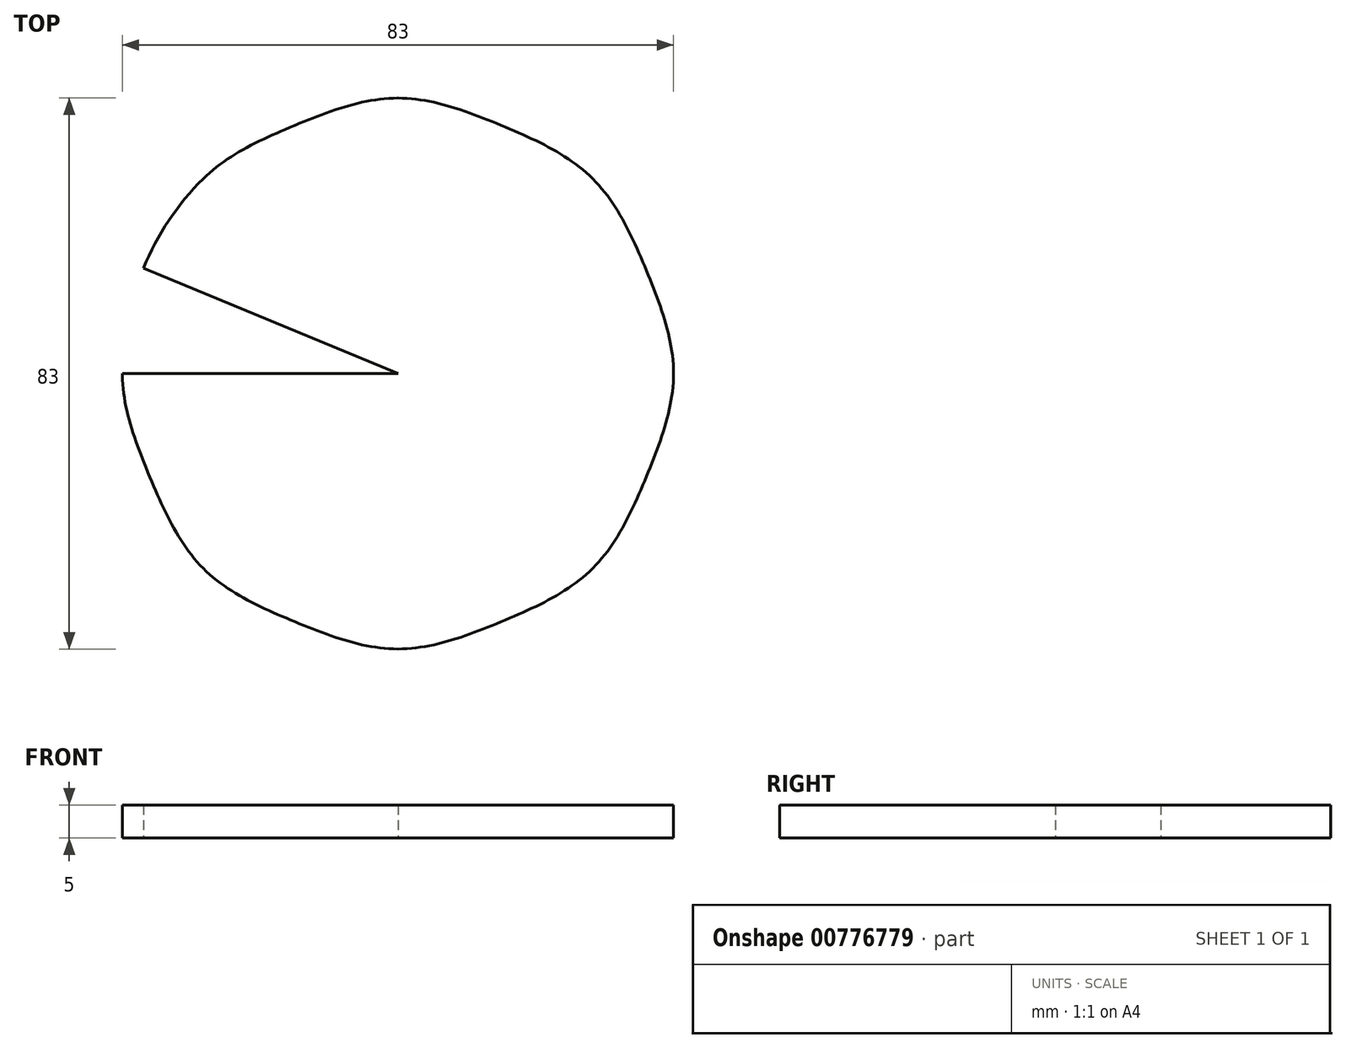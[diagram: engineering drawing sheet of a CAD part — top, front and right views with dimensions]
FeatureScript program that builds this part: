
annotation { "Feature Type Name" : "Feature", "Feature Type Description" : "" }
export const myFeature = defineFeature(function(context is Context, id is Id, definition is map)
    precondition{}
    {
        {
            var Q0;
            Q0=qCreatedBy(makeId("Top.planeOp"),FACE);
            var sketch = newSketch(context, id + "F0", { "sketchPlane" : qUnion([Q0])});
            skCircle(sketch, "E0", {"center": v(0, 0) * mm, "radius": 41.5 * mm});
            skCircle(sketch, "E1", {"center": v(0, 0) * mm, "radius": 40.5 * mm});
            skLineSegment(sketch, "E2", {"start": v(0, 0) * mm, "end": v(0, 41.5) * mm});
            skLineSegment(sketch, "E3.1.0", {"start": v(0, 0) * mm, "end": v(-15.88, 38.34) * mm});
            skLineSegment(sketch, "E3.2.0", {"start": v(0, 0) * mm, "end": v(-29.34, 29.34) * mm});
            skLineSegment(sketch, "E3.3.0", {"start": v(0, 0) * mm, "end": v(-38.34, 15.88) * mm});
            skLineSegment(sketch, "E3.4.0", {"start": v(0, 0) * mm, "end": v(-41.5, 0) * mm});
            skLineSegment(sketch, "E3.5.0", {"start": v(0, 0) * mm, "end": v(-38.34, -15.88) * mm});
            skLineSegment(sketch, "E3.6.0", {"start": v(0, 0) * mm, "end": v(-29.34, -29.34) * mm});
            skLineSegment(sketch, "E3.7.0", {"start": v(0, 0) * mm, "end": v(-15.88, -38.34) * mm});
            skLineSegment(sketch, "E3.8.0", {"start": v(0, 0) * mm, "end": v(0, -41.5) * mm});
            skLineSegment(sketch, "E3.9.0", {"start": v(0, 0) * mm, "end": v(15.88, -38.34) * mm});
            skLineSegment(sketch, "E3.10.0", {"start": v(0, 0) * mm, "end": v(29.34, -29.34) * mm});
            skLineSegment(sketch, "E3.11.0", {"start": v(0, 0) * mm, "end": v(38.34, -15.88) * mm});
            skLineSegment(sketch, "E3.12.0", {"start": v(0, 0) * mm, "end": v(41.5, 0) * mm});
            skLineSegment(sketch, "E3.13.0", {"start": v(0, 0) * mm, "end": v(38.34, 15.88) * mm});
            skLineSegment(sketch, "E3.14.0", {"start": v(0, 0) * mm, "end": v(29.34, 29.34) * mm});
            skLineSegment(sketch, "E3.15.0", {"start": v(0, 0) * mm, "end": v(15.88, 38.34) * mm});
            skFitSpline(sketch, "E4", {"points": [v(0, 41.5) * mm, v(15.5, 37.42) * mm, v(29.34, 29.34) * mm, v(37.42, 15.5) * mm, v(41.5, 0) * mm, v(37.42, -15.5) * mm, v(29.34, -29.34) * mm, v(15.5, -37.42) * mm, v(0, -41.5) * mm, v(-15.5, -37.42) * mm, v(-29.34, -29.34) * mm, v(-37.42, -15.5) * mm, v(-41.5, 0) * mm, v(-37.26, 15.88) * mm, v(-29.34, 29.34) * mm, v(-15.5, 37.42) * mm, v(0, 41.5) * mm]});
            skSolve(sketch);
        }
        {
            var Q0;
            {var subQ0=sQuery(id+"F0.wireOp",EDGE,"E4");var subQ1=sQuery(id+"F0.wireOp",EDGE,"E1");var subQ2=makeQuery(id+"F0.imprint","INTERSECT",VERTEX,{"disambiguationData":[OD(2.0)],"derivedFrom":[subQ1,subQ0]});Q0=makeQuery(id+"F0.imprint","IMPRINT",FACE,{"disambiguationData":[TD([[makeQuery(id+"F0.imprint","IMPRINT",EDGE,{"disambiguationData":[TD([[subQ2,-1.0]])],"derivedFrom":subQ1}),1.0]])]});}
            var Q1;
            {var subQ0=sQuery(id+"F0.wireOp",EDGE,"E3.2.0");var subQ1=sQuery(id+"F0.wireOp",EDGE,"E1");var subQ2=makeQuery(id+"F0.imprint","INTERSECT",VERTEX,{"derivedFrom":[subQ1,subQ0]});Q1=makeQuery(id+"F0.imprint","IMPRINT",FACE,{"disambiguationData":[TD([[makeQuery(id+"F0.imprint","IMPRINT",EDGE,{"disambiguationData":[TD([[subQ2,-1.0]])],"derivedFrom":subQ1}),1.0]])]});}
            var Q2;
            {var subQ0=sQuery(id+"F0.wireOp",EDGE,"E2");var subQ1=sQuery(id+"F0.wireOp",EDGE,"E1");var subQ2=makeQuery(id+"F0.imprint","INTERSECT",VERTEX,{"derivedFrom":[subQ1,subQ0]});Q2=makeQuery(id+"F0.imprint","IMPRINT",FACE,{"disambiguationData":[TD([[makeQuery(id+"F0.imprint","IMPRINT",EDGE,{"disambiguationData":[TD([[subQ2,-1.0]])],"derivedFrom":subQ1}),1.0]])]});}
            var Q3;
            {var subQ0=sQuery(id+"F0.wireOp",EDGE,"E4");var subQ1=sQuery(id+"F0.wireOp",EDGE,"E1");var subQ2=makeQuery(id+"F0.imprint","INTERSECT",VERTEX,{"disambiguationData":[OD(1.0)],"derivedFrom":[subQ1,subQ0]});Q3=makeQuery(id+"F0.imprint","IMPRINT",FACE,{"disambiguationData":[TD([[makeQuery(id+"F0.imprint","IMPRINT",EDGE,{"disambiguationData":[TD([[subQ2,-1.0]])],"derivedFrom":subQ1}),1.0]])]});}
            var Q4;
            {var subQ0=sQuery(id+"F0.wireOp",EDGE,"E4");var subQ1=sQuery(id+"F0.wireOp",EDGE,"E1");var subQ2=makeQuery(id+"F0.imprint","INTERSECT",VERTEX,{"disambiguationData":[OD(0.0)],"derivedFrom":[subQ1,subQ0]});Q4=makeQuery(id+"F0.imprint","IMPRINT",FACE,{"disambiguationData":[TD([[makeQuery(id+"F0.imprint","IMPRINT",EDGE,{"disambiguationData":[TD([[subQ2,-1.0]])],"derivedFrom":subQ1}),1.0]])]});}
            var Q5;
            {var subQ0=sQuery(id+"F0.wireOp",EDGE,"E3.12.0");var subQ1=sQuery(id+"F0.wireOp",EDGE,"E1");var subQ2=makeQuery(id+"F0.imprint","INTERSECT",VERTEX,{"derivedFrom":[subQ1,subQ0]});Q5=makeQuery(id+"F0.imprint","IMPRINT",FACE,{"disambiguationData":[TD([[makeQuery(id+"F0.imprint","IMPRINT",EDGE,{"disambiguationData":[TD([[subQ2,-1.0]])],"derivedFrom":subQ1}),1.0]])]});}
            var Q6;
            {var subQ0=sQuery(id+"F0.wireOp",EDGE,"E3.12.0");var subQ1=sQuery(id+"F0.wireOp",EDGE,"E1");var subQ2=makeQuery(id+"F0.imprint","INTERSECT",VERTEX,{"derivedFrom":[subQ1,subQ0]});Q6=makeQuery(id+"F0.imprint","IMPRINT",FACE,{"disambiguationData":[TD([[makeQuery(id+"F0.imprint","IMPRINT",EDGE,{"disambiguationData":[TD([[subQ2,1.0]])],"derivedFrom":subQ1}),1.0]])]});}
            var Q7;
            {var subQ0=sQuery(id+"F0.wireOp",EDGE,"E3.10.0");var subQ1=sQuery(id+"F0.wireOp",EDGE,"E1");var subQ2=makeQuery(id+"F0.imprint","INTERSECT",VERTEX,{"derivedFrom":[subQ1,subQ0]});Q7=makeQuery(id+"F0.imprint","IMPRINT",FACE,{"disambiguationData":[TD([[makeQuery(id+"F0.imprint","IMPRINT",EDGE,{"disambiguationData":[TD([[subQ2,-1.0]])],"derivedFrom":subQ1}),1.0]])]});}
            var Q8;
            {var subQ0=sQuery(id+"F0.wireOp",EDGE,"E4");var subQ1=sQuery(id+"F0.wireOp",EDGE,"E1");var subQ2=makeQuery(id+"F0.imprint","INTERSECT",VERTEX,{"disambiguationData":[OD(5.0)],"derivedFrom":[subQ1,subQ0]});Q8=makeQuery(id+"F0.imprint","IMPRINT",FACE,{"disambiguationData":[TD([[makeQuery(id+"F0.imprint","IMPRINT",EDGE,{"disambiguationData":[TD([[subQ2,-1.0]])],"derivedFrom":subQ1}),1.0]])]});}
            var Q9;
            {var subQ0=sQuery(id+"F0.wireOp",EDGE,"E3.8.0");var subQ1=sQuery(id+"F0.wireOp",EDGE,"E1");var subQ2=makeQuery(id+"F0.imprint","INTERSECT",VERTEX,{"derivedFrom":[subQ1,subQ0]});Q9=makeQuery(id+"F0.imprint","IMPRINT",FACE,{"disambiguationData":[TD([[makeQuery(id+"F0.imprint","IMPRINT",EDGE,{"disambiguationData":[TD([[subQ2,-1.0]])],"derivedFrom":subQ1}),1.0]])]});}
            var Q10;
            {var subQ0=sQuery(id+"F0.wireOp",EDGE,"E4");var subQ1=sQuery(id+"F0.wireOp",EDGE,"E1");var subQ2=makeQuery(id+"F0.imprint","INTERSECT",VERTEX,{"disambiguationData":[OD(3.0)],"derivedFrom":[subQ1,subQ0]});Q10=makeQuery(id+"F0.imprint","IMPRINT",FACE,{"disambiguationData":[TD([[makeQuery(id+"F0.imprint","IMPRINT",EDGE,{"disambiguationData":[TD([[subQ2,-1.0]])],"derivedFrom":subQ1}),1.0]])]});}
            var Q11;
            {var subQ0=sQuery(id+"F0.wireOp",EDGE,"E3.4.0");var subQ1=sQuery(id+"F0.wireOp",EDGE,"E1");var subQ2=makeQuery(id+"F0.imprint","INTERSECT",VERTEX,{"derivedFrom":[subQ1,subQ0]});Q11=makeQuery(id+"F0.imprint","IMPRINT",FACE,{"disambiguationData":[TD([[makeQuery(id+"F0.imprint","IMPRINT",EDGE,{"disambiguationData":[TD([[subQ2,-1.0]])],"derivedFrom":subQ1}),1.0]])]});}
            var Q12;
            {var subQ0=sQuery(id+"F0.wireOp",EDGE,"E4");var subQ1=sQuery(id+"F0.wireOp",EDGE,"E1");var subQ2=makeQuery(id+"F0.imprint","INTERSECT",VERTEX,{"disambiguationData":[OD(7.0)],"derivedFrom":[subQ1,subQ0]});Q12=makeQuery(id+"F0.imprint","IMPRINT",FACE,{"disambiguationData":[TD([[makeQuery(id+"F0.imprint","IMPRINT",EDGE,{"disambiguationData":[TD([[subQ2,-1.0]])],"derivedFrom":subQ1}),1.0]])]});}
            var Q13;
            {var subQ0=sQuery(id+"F0.wireOp",EDGE,"E4");var subQ1=sQuery(id+"F0.wireOp",EDGE,"E1");var subQ2=makeQuery(id+"F0.imprint","INTERSECT",VERTEX,{"disambiguationData":[OD(4.0)],"derivedFrom":[subQ1,subQ0]});Q13=makeQuery(id+"F0.imprint","IMPRINT",FACE,{"disambiguationData":[TD([[makeQuery(id+"F0.imprint","IMPRINT",EDGE,{"disambiguationData":[TD([[subQ2,-1.0]])],"derivedFrom":subQ1}),1.0]])]});}
            var Q14;
            {var subQ0=sQuery(id+"F0.wireOp",EDGE,"E3.6.0");var subQ1=sQuery(id+"F0.wireOp",EDGE,"E1");var subQ2=makeQuery(id+"F0.imprint","INTERSECT",VERTEX,{"derivedFrom":[subQ1,subQ0]});Q14=makeQuery(id+"F0.imprint","IMPRINT",FACE,{"disambiguationData":[TD([[makeQuery(id+"F0.imprint","IMPRINT",EDGE,{"disambiguationData":[TD([[subQ2,-1.0]])],"derivedFrom":subQ1}),1.0]])]});}
            var Q15;
            {var subQ0=sQuery(id+"F0.wireOp",EDGE,"E3.14.0");var subQ1=sQuery(id+"F0.wireOp",EDGE,"E1");var subQ2=makeQuery(id+"F0.imprint","INTERSECT",VERTEX,{"derivedFrom":[subQ1,subQ0]});Q15=makeQuery(id+"F0.imprint","IMPRINT",FACE,{"disambiguationData":[TD([[makeQuery(id+"F0.imprint","IMPRINT",EDGE,{"disambiguationData":[TD([[subQ2,-1.0]])],"derivedFrom":subQ1}),1.0]])]});}
            var Q16;
            {var subQ0=sQuery(id+"F0.wireOp",EDGE,"E4");var subQ1=sQuery(id+"F0.wireOp",EDGE,"E1");var subQ2=makeQuery(id+"F0.imprint","INTERSECT",VERTEX,{"disambiguationData":[OD(1.0)],"derivedFrom":[subQ1,subQ0]});Q16=makeQuery(id+"F0.imprint","IMPRINT",FACE,{"disambiguationData":[TD([[makeQuery(id+"F0.imprint","IMPRINT",EDGE,{"disambiguationData":[TD([[subQ2,-1.0]])],"derivedFrom":subQ1}),-1.0]])]});}
            var Q17;
            {var subQ0=sQuery(id+"F0.wireOp",EDGE,"E2");var subQ1=sQuery(id+"F0.wireOp",EDGE,"E1");var subQ2=makeQuery(id+"F0.imprint","INTERSECT",VERTEX,{"derivedFrom":[subQ1,subQ0]});Q17=makeQuery(id+"F0.imprint","IMPRINT",FACE,{"disambiguationData":[TD([[makeQuery(id+"F0.imprint","IMPRINT",EDGE,{"disambiguationData":[TD([[subQ2,-1.0]])],"derivedFrom":subQ1}),-1.0]])]});}
            var Q18;
            {var subQ0=sQuery(id+"F0.wireOp",EDGE,"E3.14.0");var subQ1=sQuery(id+"F0.wireOp",EDGE,"E1");var subQ2=makeQuery(id+"F0.imprint","INTERSECT",VERTEX,{"derivedFrom":[subQ1,subQ0]});Q18=makeQuery(id+"F0.imprint","IMPRINT",FACE,{"disambiguationData":[TD([[makeQuery(id+"F0.imprint","IMPRINT",EDGE,{"disambiguationData":[TD([[subQ2,-1.0]])],"derivedFrom":subQ1}),-1.0]])]});}
            var Q19;
            {var subQ0=sQuery(id+"F0.wireOp",EDGE,"E4");var subQ1=sQuery(id+"F0.wireOp",EDGE,"E1");var subQ2=makeQuery(id+"F0.imprint","INTERSECT",VERTEX,{"disambiguationData":[OD(0.0)],"derivedFrom":[subQ1,subQ0]});Q19=makeQuery(id+"F0.imprint","IMPRINT",FACE,{"disambiguationData":[TD([[makeQuery(id+"F0.imprint","IMPRINT",EDGE,{"disambiguationData":[TD([[subQ2,-1.0]])],"derivedFrom":subQ1}),-1.0]])]});}
            var Q20;
            {var subQ0=sQuery(id+"F0.wireOp",EDGE,"E3.12.0");var subQ1=sQuery(id+"F0.wireOp",EDGE,"E1");var subQ2=makeQuery(id+"F0.imprint","INTERSECT",VERTEX,{"derivedFrom":[subQ1,subQ0]});Q20=makeQuery(id+"F0.imprint","IMPRINT",FACE,{"disambiguationData":[TD([[makeQuery(id+"F0.imprint","IMPRINT",EDGE,{"disambiguationData":[TD([[subQ2,-1.0]])],"derivedFrom":subQ1}),-1.0]])]});}
            var Q21;
            {var subQ0=sQuery(id+"F0.wireOp",EDGE,"E3.12.0");var subQ1=sQuery(id+"F0.wireOp",EDGE,"E1");var subQ2=makeQuery(id+"F0.imprint","INTERSECT",VERTEX,{"derivedFrom":[subQ1,subQ0]});Q21=makeQuery(id+"F0.imprint","IMPRINT",FACE,{"disambiguationData":[TD([[makeQuery(id+"F0.imprint","IMPRINT",EDGE,{"disambiguationData":[TD([[subQ2,1.0]])],"derivedFrom":subQ1}),-1.0]])]});}
            var Q22;
            {var subQ0=sQuery(id+"F0.wireOp",EDGE,"E3.10.0");var subQ1=sQuery(id+"F0.wireOp",EDGE,"E1");var subQ2=makeQuery(id+"F0.imprint","INTERSECT",VERTEX,{"derivedFrom":[subQ1,subQ0]});Q22=makeQuery(id+"F0.imprint","IMPRINT",FACE,{"disambiguationData":[TD([[makeQuery(id+"F0.imprint","IMPRINT",EDGE,{"disambiguationData":[TD([[subQ2,-1.0]])],"derivedFrom":subQ1}),-1.0]])]});}
            var Q23;
            {var subQ0=sQuery(id+"F0.wireOp",EDGE,"E4");var subQ1=sQuery(id+"F0.wireOp",EDGE,"E1");var subQ2=makeQuery(id+"F0.imprint","INTERSECT",VERTEX,{"disambiguationData":[OD(5.0)],"derivedFrom":[subQ1,subQ0]});Q23=makeQuery(id+"F0.imprint","IMPRINT",FACE,{"disambiguationData":[TD([[makeQuery(id+"F0.imprint","IMPRINT",EDGE,{"disambiguationData":[TD([[subQ2,-1.0]])],"derivedFrom":subQ1}),-1.0]])]});}
            var Q24;
            {var subQ0=sQuery(id+"F0.wireOp",EDGE,"E3.8.0");var subQ1=sQuery(id+"F0.wireOp",EDGE,"E1");var subQ2=makeQuery(id+"F0.imprint","INTERSECT",VERTEX,{"derivedFrom":[subQ1,subQ0]});Q24=makeQuery(id+"F0.imprint","IMPRINT",FACE,{"disambiguationData":[TD([[makeQuery(id+"F0.imprint","IMPRINT",EDGE,{"disambiguationData":[TD([[subQ2,-1.0]])],"derivedFrom":subQ1}),-1.0]])]});}
            var Q25;
            {var subQ0=sQuery(id+"F0.wireOp",EDGE,"E4");var subQ1=sQuery(id+"F0.wireOp",EDGE,"E1");var subQ2=makeQuery(id+"F0.imprint","INTERSECT",VERTEX,{"disambiguationData":[OD(4.0)],"derivedFrom":[subQ1,subQ0]});Q25=makeQuery(id+"F0.imprint","IMPRINT",FACE,{"disambiguationData":[TD([[makeQuery(id+"F0.imprint","IMPRINT",EDGE,{"disambiguationData":[TD([[subQ2,-1.0]])],"derivedFrom":subQ1}),-1.0]])]});}
            var Q26;
            {var subQ0=sQuery(id+"F0.wireOp",EDGE,"E3.6.0");var subQ1=sQuery(id+"F0.wireOp",EDGE,"E1");var subQ2=makeQuery(id+"F0.imprint","INTERSECT",VERTEX,{"derivedFrom":[subQ1,subQ0]});Q26=makeQuery(id+"F0.imprint","IMPRINT",FACE,{"disambiguationData":[TD([[makeQuery(id+"F0.imprint","IMPRINT",EDGE,{"disambiguationData":[TD([[subQ2,-1.0]])],"derivedFrom":subQ1}),-1.0]])]});}
            var Q27;
            {var subQ0=sQuery(id+"F0.wireOp",EDGE,"E4");var subQ1=sQuery(id+"F0.wireOp",EDGE,"E1");var subQ2=makeQuery(id+"F0.imprint","INTERSECT",VERTEX,{"disambiguationData":[OD(3.0)],"derivedFrom":[subQ1,subQ0]});Q27=makeQuery(id+"F0.imprint","IMPRINT",FACE,{"disambiguationData":[TD([[makeQuery(id+"F0.imprint","IMPRINT",EDGE,{"disambiguationData":[TD([[subQ2,-1.0]])],"derivedFrom":subQ1}),-1.0]])]});}
            var Q28;
            {var subQ0=sQuery(id+"F0.wireOp",EDGE,"E3.4.0");var subQ1=sQuery(id+"F0.wireOp",EDGE,"E1");var subQ2=makeQuery(id+"F0.imprint","INTERSECT",VERTEX,{"derivedFrom":[subQ1,subQ0]});Q28=makeQuery(id+"F0.imprint","IMPRINT",FACE,{"disambiguationData":[TD([[makeQuery(id+"F0.imprint","IMPRINT",EDGE,{"disambiguationData":[TD([[subQ2,-1.0]])],"derivedFrom":subQ1}),-1.0]])]});}
            var Q29;
            {var subQ0=sQuery(id+"F0.wireOp",EDGE,"E4");var subQ1=sQuery(id+"F0.wireOp",EDGE,"E1");var subQ2=makeQuery(id+"F0.imprint","INTERSECT",VERTEX,{"disambiguationData":[OD(7.0)],"derivedFrom":[subQ1,subQ0]});Q29=makeQuery(id+"F0.imprint","IMPRINT",FACE,{"disambiguationData":[TD([[makeQuery(id+"F0.imprint","IMPRINT",EDGE,{"disambiguationData":[TD([[subQ2,-1.0]])],"derivedFrom":subQ1}),-1.0]])]});}
            var Q30;
            {var subQ0=sQuery(id+"F0.wireOp",EDGE,"E3.2.0");var subQ1=sQuery(id+"F0.wireOp",EDGE,"E1");var subQ2=makeQuery(id+"F0.imprint","INTERSECT",VERTEX,{"derivedFrom":[subQ1,subQ0]});Q30=makeQuery(id+"F0.imprint","IMPRINT",FACE,{"disambiguationData":[TD([[makeQuery(id+"F0.imprint","IMPRINT",EDGE,{"disambiguationData":[TD([[subQ2,-1.0]])],"derivedFrom":subQ1}),-1.0]])]});}
            var Q31;
            {var subQ0=sQuery(id+"F0.wireOp",EDGE,"E4");var subQ1=sQuery(id+"F0.wireOp",EDGE,"E1");var subQ2=makeQuery(id+"F0.imprint","INTERSECT",VERTEX,{"disambiguationData":[OD(2.0)],"derivedFrom":[subQ1,subQ0]});Q31=makeQuery(id+"F0.imprint","IMPRINT",FACE,{"disambiguationData":[TD([[makeQuery(id+"F0.imprint","IMPRINT",EDGE,{"disambiguationData":[TD([[subQ2,-1.0]])],"derivedFrom":subQ1}),-1.0]])]});}
            var Q32;
            Q32=sQuery(id+"F0.wireOp",EDGE,"E4");
            extrude(context, id + "F1", {"entities" : qUnion([Q0, Q1, Q2, Q3, Q4, Q5, Q6, Q7, Q8, Q9, Q10, Q11, Q12, Q13, Q14, Q15, Q16, Q17, Q18, Q19, Q20, Q21, Q22, Q23, Q24, Q25, Q26, Q27, Q28, Q29, Q30, Q31]), "surfaceOperationType" : NewSurfaceOperationType.ADD, "surfaceEntities" : qUnion([Q32]), "depth" : 5 * mm, "offsetDistance" : 25 * mm});
        }
    });
